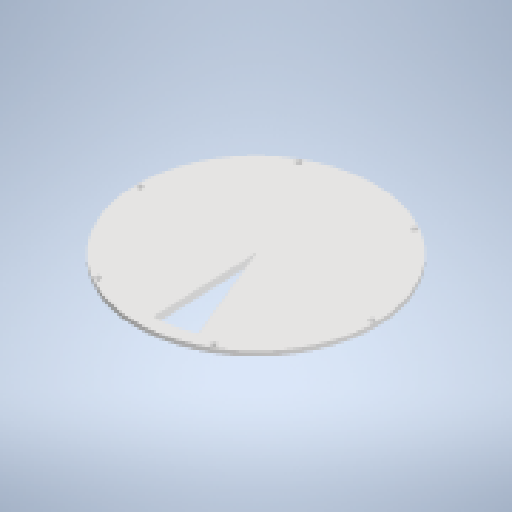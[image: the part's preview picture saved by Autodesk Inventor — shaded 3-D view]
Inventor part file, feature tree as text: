
AUTODESK INVENTOR PART (.ipt)
format: ipt  version: 2025 (Build 290162010, 162A)  size: 160,256 bytes
history: native  units: mm
features: sketch x4, reference x4, other x4, extrude x2, hole x1, chamfer x1
ambient origin geometry x8: Origin, YZ Plane, XZ Plane, XY Plane, X Axis, Y Axis, Z Axis, Center Point
bodies: Volumenkörper1 (feature_tree)
feature tree (16):
  extrude  "Extrusion1"  Depth=3.0mm
  hole  "Bohrung1"  [1 undecoded]
  extrude  "Extrusion2"  [1 undecoded]
  chamfer  "Fasen1"  [1 undecoded]
  sketch  "Skizze1"  dims[d0=3.0mm d1=0.0mm d2=78.5mm]
  reference  "Referenz1"
  sketch  "Skizze2"  dims[d7=2.4mm d8=6.0mm d9=4.4mm d10=2.0mm d11=90.0deg d12=8.0mm d13=20.594885mm d14=0.0mm d15=0.0mm]
  sketch  "Skizze - Runde Anordnung1"  dims[d3=60.0mm d5=360.0deg]
  sketch  "Skizze3"  dims[d16=2.0mm d17=3.0mm d18=45.0deg]
  reference  "Referenz2"
  reference  "Referenz4"
  reference  "Referenz5"
  other  "<userpath>\GIT\pillbox\Baugruppe1.iam"
  other  "Baugruppe1.iam"
  other  "Bauteil2:1"
  other  "Bauteil1:1"
note: 3 required parameter values undecoded (feature->parameter linkage not recoverable at this tier; creation-order binding heuristic only, values carry confidence <= 0.55)
